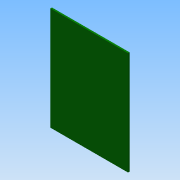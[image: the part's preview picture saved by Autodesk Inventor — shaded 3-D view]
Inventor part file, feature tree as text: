
AUTODESK INVENTOR PART (.ipt)
format: ipt  version: 2015 (Build 190159000, 159)  size: 74,240 bytes
history: native  units: in
note: dims shown in document units (in); Inventor stores cm internally (conversion verified against a paired STEP export)
features: reference x4, extrude x1, sketch x1
ambient origin geometry x8: Origin, YZ Plane, XZ Plane, XY Plane, X Axis, Y Axis, Z Axis, Center Point
bodies: Solid1 (feature_tree)
feature tree (6):
  extrude  "Extrusion1"  Depth=0.1in TaperAngle=0.0deg
  sketch  "Sketch1"  dims[d1=0.5in d2=0.1in d3=0.0in d4=0.5in]
  reference  "Reference1"
  reference  "Reference3"
  reference  "Reference4"
  reference  "Reference5"
